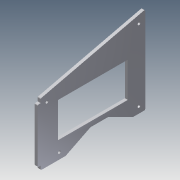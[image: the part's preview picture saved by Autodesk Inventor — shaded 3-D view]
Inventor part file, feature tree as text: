
AUTODESK INVENTOR PART (.ipt)
format: ipt  version: 2014 (Build 180170000, 170)  size: 164,352 bytes
history: native  units: mm
features: extrude x6, sketch x6, fillet x1
ambient origin geometry x8: Origin, YZ Plane, XZ Plane, XY Plane, X Axis, Y Axis, Z Axis, Center Point
bodies: Solid1 (feature_tree)
feature tree (13):
  extrude  "Extrusion1"  Depth=210.0mm
  extrude  "Extrusion2"  Depth=25.0mm
  extrude  "Extrusion3"  Depth=6.0mm TaperAngle=0.0deg
  extrude  "Extrusion4"  Depth=3.0mm TaperAngle=0.0deg
  extrude  "Extrusion5"  Depth=8.1mm
  fillet  "Fillet1"  Radius=6.0mm
  extrude  "Extrusion6"  Depth=2.0mm
  sketch  "Sketch1"  dims[d0=150.0mm d1=210.0mm]
  sketch  "Sketch2"  dims[d2=6.0mm d3=0.0mm d4=25.0mm]
  sketch  "Sketch3"  dims[d5=50.0mm d6=6.0mm d7=0.0mm]
  sketch  "Sketch4"  dims[d8=50.0mm d9=3.0mm d10=0.0mm]
  sketch  "Sketch5"  dims[d11=8.1mm d12=8.1mm d13=6.0mm]
  sketch  "Sketch6"  dims[d14=6.0mm d15=0.0mm d16=2.0mm d17=12.5mm d18=12.5mm d19=12.5mm d21=5.4mm d22=37.5mm d23=6.0mm d24=0.0mm d25=50.0mm d26=12.5mm d27=10.0mm d28=35.0mm d29=35.0mm d30=70.0mm d31=6.0mm d32=0.0mm]
